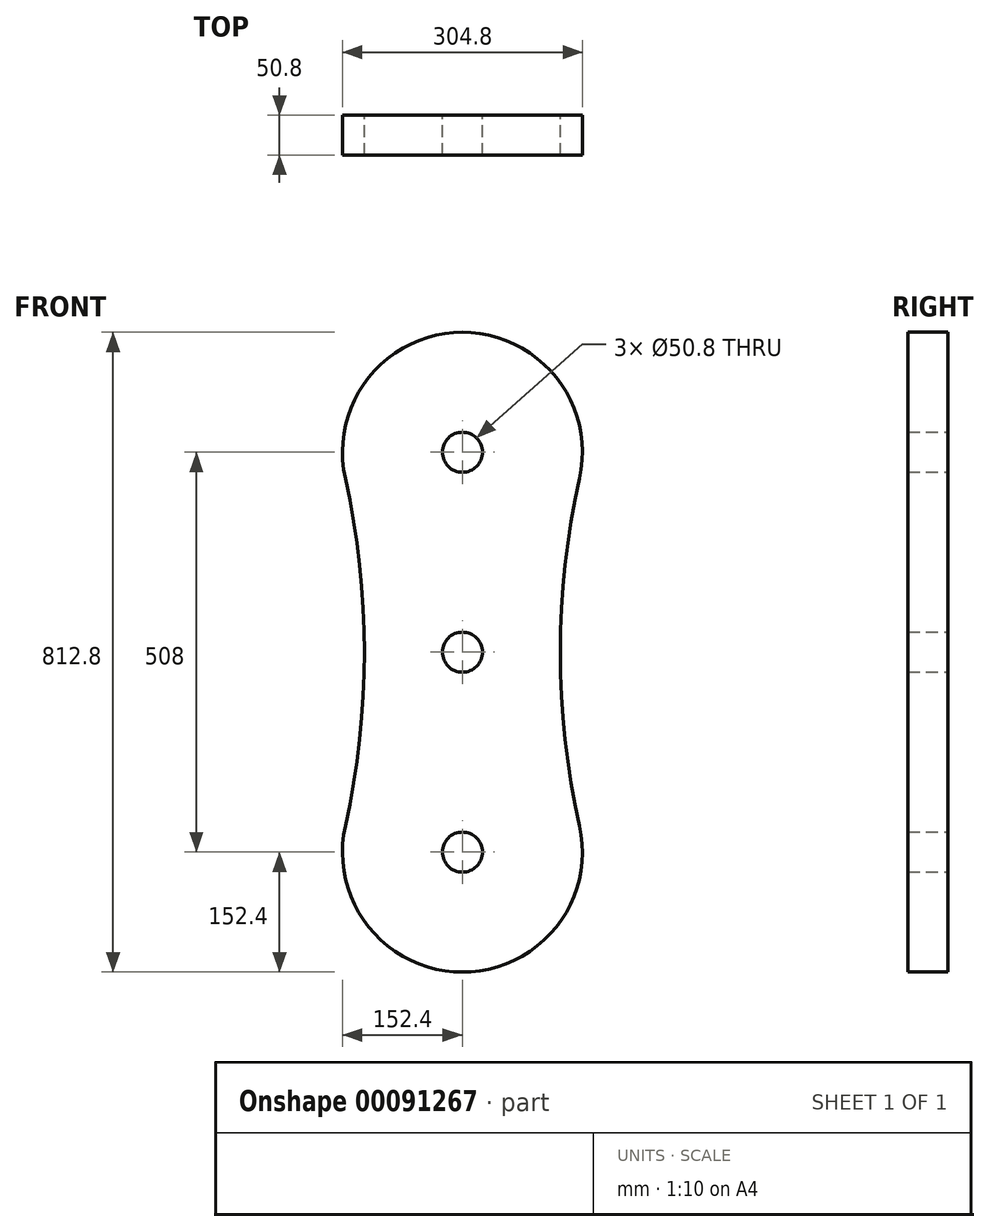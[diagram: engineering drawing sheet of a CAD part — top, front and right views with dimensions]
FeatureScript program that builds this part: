
annotation { "Feature Type Name" : "Feature", "Feature Type Description" : "" }
export const myFeature = defineFeature(function(context is Context, id is Id, definition is map)
    precondition{}
    {
        {
            var Q0;
            Q0=qCreatedBy(makeId("Front.planeOp"),FACE);
            var sketch = newSketch(context, id + "F0", { "sketchPlane" : qUnion([Q0])});
            skArc(sketch, "E0", {"start": v(-148.76, 33.13) * mm, "mid": v(0, -152.4) * mm, "end": v(148.76, 33.13) * mm});
            skArc(sketch, "E1", {"start": v(148.76, 474.87) * mm, "mid": v(0, 660.4) * mm, "end": v(-148.76, 474.87) * mm});
            skArc(sketch, "E2", {"start": v(-148.76, 33.13) * mm, "mid": v(-124.46, 254) * mm, "end": v(-148.76, 474.87) * mm});
            skArc(sketch, "E3", {"start": v(148.76, 474.87) * mm, "mid": v(124.46, 254) * mm, "end": v(148.76, 33.13) * mm});
            skCircle(sketch, "E4", {"center": v(0, 0) * mm, "radius": 25.4 * mm});
            skCircle(sketch, "E5", {"center": v(0, 508) * mm, "radius": 25.4 * mm});
            skCircle(sketch, "E6", {"center": v(0, 254) * mm, "radius": 25.4 * mm});
            skSolve(sketch);
        }
        {
            var Q0;
            Q0=makeQuery(id+"F0.imprint","IMPRINT",FACE,{"disambiguationData":[TD([[makeQuery(id+"F0.imprint","IMPRINT",EDGE,{"derivedFrom":sQuery(id+"F0.wireOp",EDGE,"E0")}),1.0]])]});
            extrude(context, id + "F1", {"entities" : qUnion([Q0]), "depth" : 50.8 * mm});
        }
    });
